# Revit family: NBS_DudleyIndustries_LittrBins_PlatinumRange_WasteBin14Litre
name_source: partatom
category: Generic Models
revit_build: Autodesk Revit 2016 (Build: 20150220_1215(x64)
units: mm (PartAtom-declared; Revit-internal decimal feet)

## family parameters
Always vertical = Yes
Can host rebar = No
Cut with Voids When Loaded = No
OmniClass Number = 23.40.20.31.11
OmniClass Title = Bins
Part Type = Normal
Room Calculation Point = No
Round Connector Dimension = Use Diameter
Shared = No
Work Plane-Based = No

## types (1)
- PlatinumRangeWasteBin14Litre
    AssetType = Movable
    BIMObjectName = NBS_DudleyIndustries_LitterBins_PlatinumRange_WasteBin14Litre
    BinMaterial = NBS_Concept
    Category = Pr_40_50_07_47:Litter bins
    Color = Stainless Steel
    ColourOptions = Stainless steel
    Description = Free standing or wall mounted 14 litre waste bin,  with internal plastic liner
    DurationUnit = year
    ExpectedLife = 5
    Features = Sleek and contemporary design, simple to wipe clean and finger print resistant, solid durable construction, free standing or wall mounted for extra security
    Finish = Brushed/Lacquered (77004CB)
    FinishAsDelivered = Brushed/Lacquered (77004CB)
    IfcExportAs = IfcBuildingElementProxyType
    IfcExportType = NOTDEFINED
    MainColor = Stainless Steel
    ManufacturerName = Dudley Industries
    ManufacturerURL = www.dudleyindustries.com/
    Material = Stainless Steel
    ModelNumber = 77004
    ModelReference = Platinum range: Waste Bin 14 Litre
    NBSCertification = www.nationalbimlibrary.com/cert/ezdzedeu
    NBSDescription = Litter bins
    NBSReference = 45-35-86/335
    Name = LitterBins_PlatinumRange_WasteBin14Litre_DudleyIndustries
    NominalDepth = 215 mm  [stored 0.705381 ft]
    NominalHeight = 410 mm  [stored 1.34514 ft]
    NominalLength = 275 mm  [stored 0.902231 ft]
    NominalWidth = 215 mm  [stored 0.705381 ft]
    ProductInformation = www.dudleyindustries.com/wp-content/uploads/2017/08/Platinum_14_Litre_Waste_Bin.pdf
    Size = 275 x 410 x 215 mm
    Style = Sleek and contemporary design
    Uniclass2015Code = Pr_40_50_07_47
    Uniclass2015Title = Litter bins
    Uniclass2015Version = Products v1.7
    Version = 2
    WarrantyDescription = 1 year warranty
    WarrantyDurationParts = 1
    WarrantyDurationUnit = year

note: [stored X ft] marks values corroborated as IEEE doubles in the binary element streams (Revit-internal decimal feet)

## geometry (parser evidence)
native form markers: Sweep x2
no freeform markers — native parametric forms only
